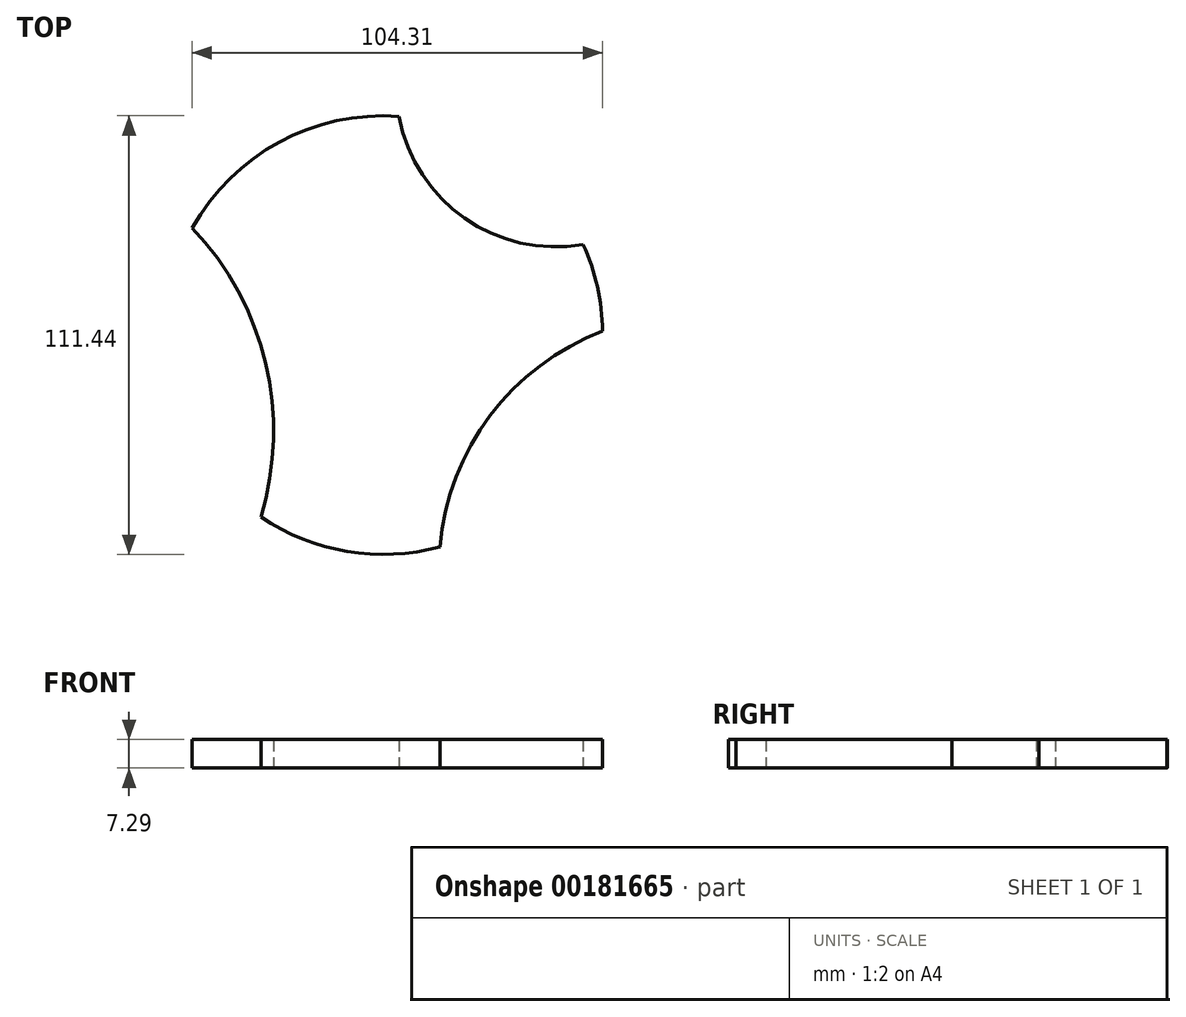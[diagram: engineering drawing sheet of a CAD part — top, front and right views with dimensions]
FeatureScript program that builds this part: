
annotation { "Feature Type Name" : "Feature", "Feature Type Description" : "" }
export const myFeature = defineFeature(function(context is Context, id is Id, definition is map)
    precondition{}
    {
        {
            var Q0;
            Q0=qCreatedBy(makeId("Top.planeOp"),FACE);
            var sketch = newSketch(context, id + "F0", { "sketchPlane" : qUnion([Q0])});
            skArc(sketch, "E0", {"start": v(-31.14, -46.2) * mm, "mid": v(-9.21, -54.95) * mm, "end": v(14.37, -53.83) * mm});
            skArc(sketch, "E1", {"start": v(3.96, 55.58) * mm, "mid": v(20.65, 29.69) * mm, "end": v(50.73, 23.04) * mm});
            skArc(sketch, "E2", {"start": v(-31.14, -46.2) * mm, "mid": v(-29.92, -7.12) * mm, "end": v(-48.6, 27.24) * mm});
            skArc(sketch, "E3", {"start": v(55.7, 1.01) * mm, "mid": v(27.13, -20.45) * mm, "end": v(14.37, -53.83) * mm});
            skArc(sketch, "E4.trimOffspring", {"start": v(3.96, 55.58) * mm, "mid": v(-26.44, 49.05) * mm, "end": v(-48.6, 27.24) * mm});
            skArc(sketch, "E5.trimOffspring", {"start": v(55.7, 1.01) * mm, "mid": v(54.35, 12.28) * mm, "end": v(50.73, 23.04) * mm});
            skSolve(sketch);
        }
        {
            var Q0;
            Q0=makeQuery(id+"F0.imprint","IMPRINT",FACE,{"disambiguationData":[TD([[makeQuery(id+"F0.imprint","IMPRINT",EDGE,{"derivedFrom":sQuery(id+"F0.wireOp",EDGE,"E0")}),1.0]])]});
            extrude(context, id + "F1", {"entities" : qUnion([Q0]), "depth" : 7.3 * mm});
        }
    });
